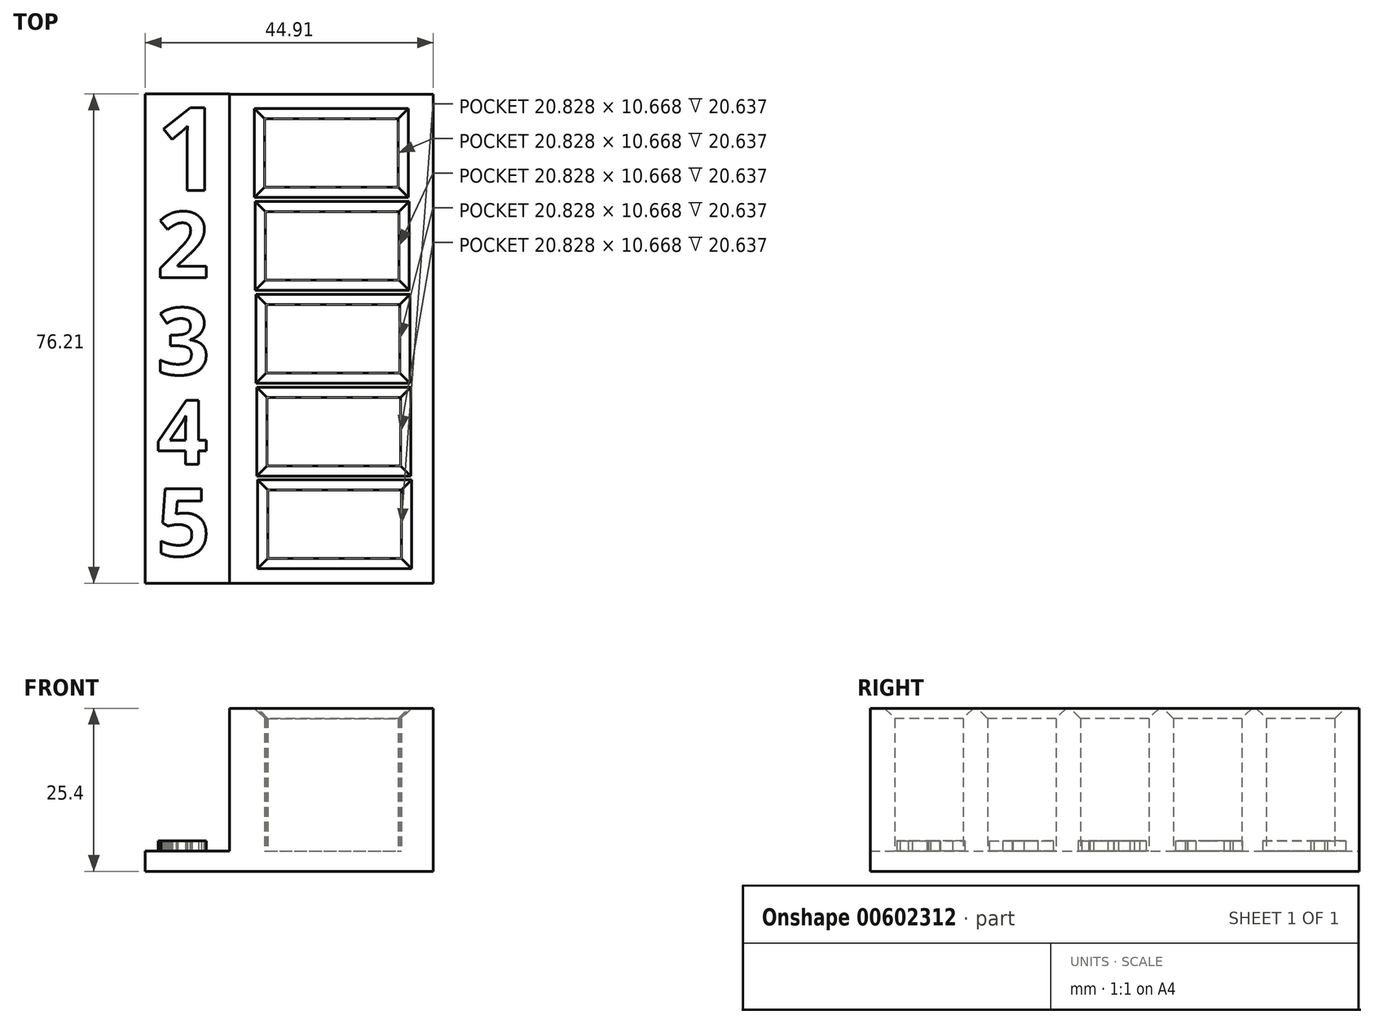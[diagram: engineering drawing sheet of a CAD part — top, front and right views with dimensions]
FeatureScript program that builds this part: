
annotation { "Feature Type Name" : "Feature", "Feature Type Description" : "" }
export const myFeature = defineFeature(function(context is Context, id is Id, definition is map)
    precondition{}
    {
        {
            var Q0;
            Q0=qCreatedBy(makeId("Top.planeOp"),FACE);
            var sketch = newSketch(context, id + "F0", { "sketchPlane" : qUnion([Q0])});
            skLineSegment(sketch, "E0.top", {"start": v(0, 76.2) * mm, "end": v(31.75, 76.2) * mm});
            skLineSegment(sketch, "E0.left", {"start": v(0, 0) * mm, "end": v(0, 76.2) * mm});
            skLineSegment(sketch, "E0.right", {"start": v(31.75, 0) * mm, "end": v(31.75, 76.2) * mm});
            skLineSegment(sketch, "E1.bottom", {"start": v(5.46, 72.4) * mm, "end": v(26.29, 72.4) * mm});
            skLineSegment(sketch, "E1.top", {"start": v(5.46, 61.72) * mm, "end": v(26.29, 61.72) * mm});
            skLineSegment(sketch, "E1.left", {"start": v(5.46, 72.4) * mm, "end": v(5.46, 61.72) * mm});
            skLineSegment(sketch, "E1.right", {"start": v(26.29, 72.4) * mm, "end": v(26.29, 61.72) * mm});
            skLineSegment(sketch, "E2", {"start": v(0, 0) * mm, "end": v(31.75, 0) * mm});
            skLineSegment(sketch, "E3.1.0.0", {"start": v(26.42, 57.91) * mm, "end": v(26.42, 47.24) * mm});
            skLineSegment(sketch, "E3.1.0.1", {"start": v(5.59, 57.91) * mm, "end": v(5.59, 47.24) * mm});
            skLineSegment(sketch, "E3.1.0.2", {"start": v(5.59, 47.24) * mm, "end": v(26.42, 47.24) * mm});
            skLineSegment(sketch, "E3.1.0.3", {"start": v(5.59, 57.91) * mm, "end": v(26.42, 57.91) * mm});
            skLineSegment(sketch, "E3.2.0.0", {"start": v(26.54, 43.44) * mm, "end": v(26.54, 32.77) * mm});
            skLineSegment(sketch, "E3.2.0.1", {"start": v(5.71, 43.44) * mm, "end": v(5.71, 32.77) * mm});
            skLineSegment(sketch, "E3.2.0.2", {"start": v(5.71, 32.77) * mm, "end": v(26.54, 32.77) * mm});
            skLineSegment(sketch, "E3.2.0.3", {"start": v(5.71, 43.44) * mm, "end": v(26.54, 43.44) * mm});
            skLineSegment(sketch, "E3.3.0.0", {"start": v(26.67, 28.96) * mm, "end": v(26.67, 18.29) * mm});
            skLineSegment(sketch, "E3.3.0.1", {"start": v(5.84, 28.96) * mm, "end": v(5.84, 18.29) * mm});
            skLineSegment(sketch, "E3.3.0.2", {"start": v(5.84, 18.29) * mm, "end": v(26.67, 18.29) * mm});
            skLineSegment(sketch, "E3.3.0.3", {"start": v(5.84, 28.96) * mm, "end": v(26.67, 28.96) * mm});
            skLineSegment(sketch, "E3.4.0.0", {"start": v(26.8, 14.48) * mm, "end": v(26.8, 3.81) * mm});
            skLineSegment(sketch, "E3.4.0.1", {"start": v(5.97, 14.48) * mm, "end": v(5.97, 3.81) * mm});
            skLineSegment(sketch, "E3.4.0.2", {"start": v(5.97, 3.81) * mm, "end": v(26.8, 3.81) * mm});
            skLineSegment(sketch, "E3.4.0.3", {"start": v(5.97, 14.48) * mm, "end": v(26.8, 14.48) * mm});
            skLineSegment(sketch, "E3.direction1", {"start": v(5.46, 61.72) * mm, "end": v(5.59, 47.24) * mm, "construction": true});
            skSolve(sketch);
        }
        {
            var Q0;
            Q0=makeQuery(id+"F0.imprint","IMPRINT",FACE,{"disambiguationData":[TD([[makeQuery(id+"F0.imprint","IMPRINT",EDGE,{"derivedFrom":sQuery(id+"F0.wireOp",EDGE,"E0.top")}),-1.0]])]});
            extrude(context, id + "F1", {"entities" : qUnion([Q0]), "depth" : 25.4 * mm, "offsetDistance" : 25.4 * mm});
        }
        {
            var Q0;
            Q0=qCreatedBy(makeId("Top.planeOp"),FACE);
            var sketch = newSketch(context, id + "F2", { "sketchPlane" : qUnion([Q0])});
            skLineSegment(sketch, "E4.bottom", {"start": v(31.7, 0) * mm, "end": v(-13.16, 0) * mm});
            skLineSegment(sketch, "E4.top", {"start": v(31.7, 76.2) * mm, "end": v(-13.16, 76.2) * mm});
            skLineSegment(sketch, "E4.left", {"start": v(31.7, 0) * mm, "end": v(31.7, 76.2) * mm});
            skLineSegment(sketch, "E4.right", {"start": v(-13.16, 0) * mm, "end": v(-13.16, 76.2) * mm});
            skSolve(sketch);
        }
        {
            var Q0;
            Q0=makeQuery(id+"F2.imprint","IMPRINT",FACE,{"disambiguationData":[TD([[makeQuery(id+"F2.imprint","IMPRINT",EDGE,{"derivedFrom":sQuery(id+"F2.wireOp",EDGE,"E4.bottom")}),-1.0]])]});
            extrude(context, id + "F3", {"entities" : qUnion([Q0]), "operationType" : NewBodyOperationType.ADD, "depth" : 3.17 * mm, "offsetDistance" : 25.4 * mm});
        }
        {
            var Q0;
            {var subQ0=sQuery(id+"F2.wireOp",EDGE,"E4.bottom");var subQ1=sQuery(id+"F2.wireOp",EDGE,"E4.top");var subQ2=sQuery(id+"F2.wireOp",EDGE,"E4.left");var subQ3=sQuery(id+"F2.wireOp",EDGE,"E4.right");Q0=makeQuery(id+"F3.boolean.opBoolean","SPLIT",FACE,{"disambiguationData":[TD([makeQuery(id+"F1.opExtrude","SWEPT_FACE",FACE,{"disambiguationData":[OSD([sQuery(id+"F0.wireOp",EDGE,"E0.top")])]})])],"derivedFrom":makeQuery(id+"F3.opExtrude","CAP_FACE",FACE,{"disambiguationData":[OSD([subQ0,subQ1,subQ2,subQ3])],"isStart":false})});}
            var sketch = newSketch(context, id + "F4", { "sketchPlane" : qUnion([Q0])});
            skLineSegment(sketch, "E5", {"start": v(-11.38, 76.2) * mm, "end": v(-11.38, -11.79) * mm, "construction": true});
            skLineSegment(sketch, "E6", {"start": v(-2.72, -11.79) * mm, "end": v(-2.72, 81.55) * mm, "construction": true});
            skText(sketch, "E7", { "text": "1", "fontName": "OpenSans-Bold.ttf"});
            skText(sketch, "E8", { "text": "2", "fontName": "OpenSans-Bold.ttf"});
            skText(sketch, "E9", { "text": "3", "fontName": "OpenSans-Bold.ttf"});
            skText(sketch, "E10", { "text": "4", "fontName": "OpenSans-Bold.ttf"});
            skText(sketch, "E11", { "text": "5", "fontName": "OpenSans-Bold.ttf"});
            const initialGuessF4  = {"E7": [-0.01138, 0.06116, 1, 0, 0.01304], "E8": [-0.01138, 0.04757, 1, 0, 0.01032], "E9": [-0.01138, 0.0325, 1, 0, 0.01044], "E10": [-0.01138, 0.01853, 1, 0, 0.01006], "E11": [-0.01138, 0.00423, 1, 0, 0.01055]};
            skSetInitialGuess(sketch, initialGuessF4);
            skSolve(sketch);
        }
        {
            var Q0;
            Q0 = qSketchRegion(id + "F4", true);
            extrude(context, id + "F5", {"entities" : qUnion([Q0]), "operationType" : NewBodyOperationType.ADD, "depth" : 1.59 * mm, "offsetDistance" : 25.4 * mm});
        }
        {
            var Q0;
            Q0=makeQuery(id+"F1.opExtrude","CAP_EDGE",EDGE,{"disambiguationData":[OSD([sQuery(id+"F0.wireOp",EDGE,"E3.4.0.1")])],"isStart":false});
            var Q1;
            Q1=makeQuery(id+"F1.opExtrude","CAP_EDGE",EDGE,{"disambiguationData":[OSD([sQuery(id+"F0.wireOp",EDGE,"E3.4.0.2")])],"isStart":false});
            var Q2;
            Q2=makeQuery(id+"F1.opExtrude","CAP_EDGE",EDGE,{"disambiguationData":[OSD([sQuery(id+"F0.wireOp",EDGE,"E3.4.0.0")])],"isStart":false});
            var Q3;
            Q3=makeQuery(id+"F1.opExtrude","CAP_EDGE",EDGE,{"disambiguationData":[OSD([sQuery(id+"F0.wireOp",EDGE,"E3.4.0.3")])],"isStart":false});
            var Q4;
            Q4=makeQuery(id+"F1.opExtrude","CAP_EDGE",EDGE,{"disambiguationData":[OSD([sQuery(id+"F0.wireOp",EDGE,"E3.3.0.2")])],"isStart":false});
            var Q5;
            Q5=makeQuery(id+"F1.opExtrude","CAP_EDGE",EDGE,{"disambiguationData":[OSD([sQuery(id+"F0.wireOp",EDGE,"E3.3.0.1")])],"isStart":false});
            var Q6;
            Q6=makeQuery(id+"F1.opExtrude","CAP_EDGE",EDGE,{"disambiguationData":[OSD([sQuery(id+"F0.wireOp",EDGE,"E3.3.0.0")])],"isStart":false});
            var Q7;
            Q7=makeQuery(id+"F1.opExtrude","CAP_EDGE",EDGE,{"disambiguationData":[OSD([sQuery(id+"F0.wireOp",EDGE,"E3.3.0.3")])],"isStart":false});
            var Q8;
            Q8=makeQuery(id+"F1.opExtrude","CAP_EDGE",EDGE,{"disambiguationData":[OSD([sQuery(id+"F0.wireOp",EDGE,"E3.2.0.2")])],"isStart":false});
            var Q9;
            Q9=makeQuery(id+"F1.opExtrude","CAP_EDGE",EDGE,{"disambiguationData":[OSD([sQuery(id+"F0.wireOp",EDGE,"E3.2.0.1")])],"isStart":false});
            var Q10;
            Q10=makeQuery(id+"F1.opExtrude","CAP_EDGE",EDGE,{"disambiguationData":[OSD([sQuery(id+"F0.wireOp",EDGE,"E3.2.0.0")])],"isStart":false});
            var Q11;
            Q11=makeQuery(id+"F1.opExtrude","CAP_EDGE",EDGE,{"disambiguationData":[OSD([sQuery(id+"F0.wireOp",EDGE,"E3.2.0.3")])],"isStart":false});
            var Q12;
            Q12=makeQuery(id+"F1.opExtrude","CAP_EDGE",EDGE,{"disambiguationData":[OSD([sQuery(id+"F0.wireOp",EDGE,"E3.1.0.3")])],"isStart":false});
            var Q13;
            Q13=makeQuery(id+"F1.opExtrude","CAP_EDGE",EDGE,{"disambiguationData":[OSD([sQuery(id+"F0.wireOp",EDGE,"E3.1.0.1")])],"isStart":false});
            var Q14;
            Q14=makeQuery(id+"F1.opExtrude","CAP_EDGE",EDGE,{"disambiguationData":[OSD([sQuery(id+"F0.wireOp",EDGE,"E3.1.0.2")])],"isStart":false});
            var Q15;
            Q15=makeQuery(id+"F1.opExtrude","CAP_EDGE",EDGE,{"disambiguationData":[OSD([sQuery(id+"F0.wireOp",EDGE,"E3.1.0.0")])],"isStart":false});
            var Q16;
            Q16=makeQuery(id+"F1.opExtrude","CAP_EDGE",EDGE,{"disambiguationData":[OSD([sQuery(id+"F0.wireOp",EDGE,"E1.top")])],"isStart":false});
            var Q17;
            Q17=makeQuery(id+"F1.opExtrude","CAP_EDGE",EDGE,{"disambiguationData":[OSD([sQuery(id+"F0.wireOp",EDGE,"E1.left")])],"isStart":false});
            var Q18;
            Q18=makeQuery(id+"F1.opExtrude","CAP_EDGE",EDGE,{"disambiguationData":[OSD([sQuery(id+"F0.wireOp",EDGE,"E1.bottom")])],"isStart":false});
            var Q19;
            Q19=makeQuery(id+"F1.opExtrude","CAP_EDGE",EDGE,{"disambiguationData":[OSD([sQuery(id+"F0.wireOp",EDGE,"E1.right")])],"isStart":false});
            chamfer(context, id + "F6", {"entities" : qUnion([Q0, Q1, Q2, Q3, Q4, Q5, Q6, Q7, Q8, Q9, Q10, Q11, Q12, Q13, Q14, Q15, Q16, Q17, Q18, Q19]), "width" : 1.59 * mm, "tangentPropagation" : true});
        }
    });
